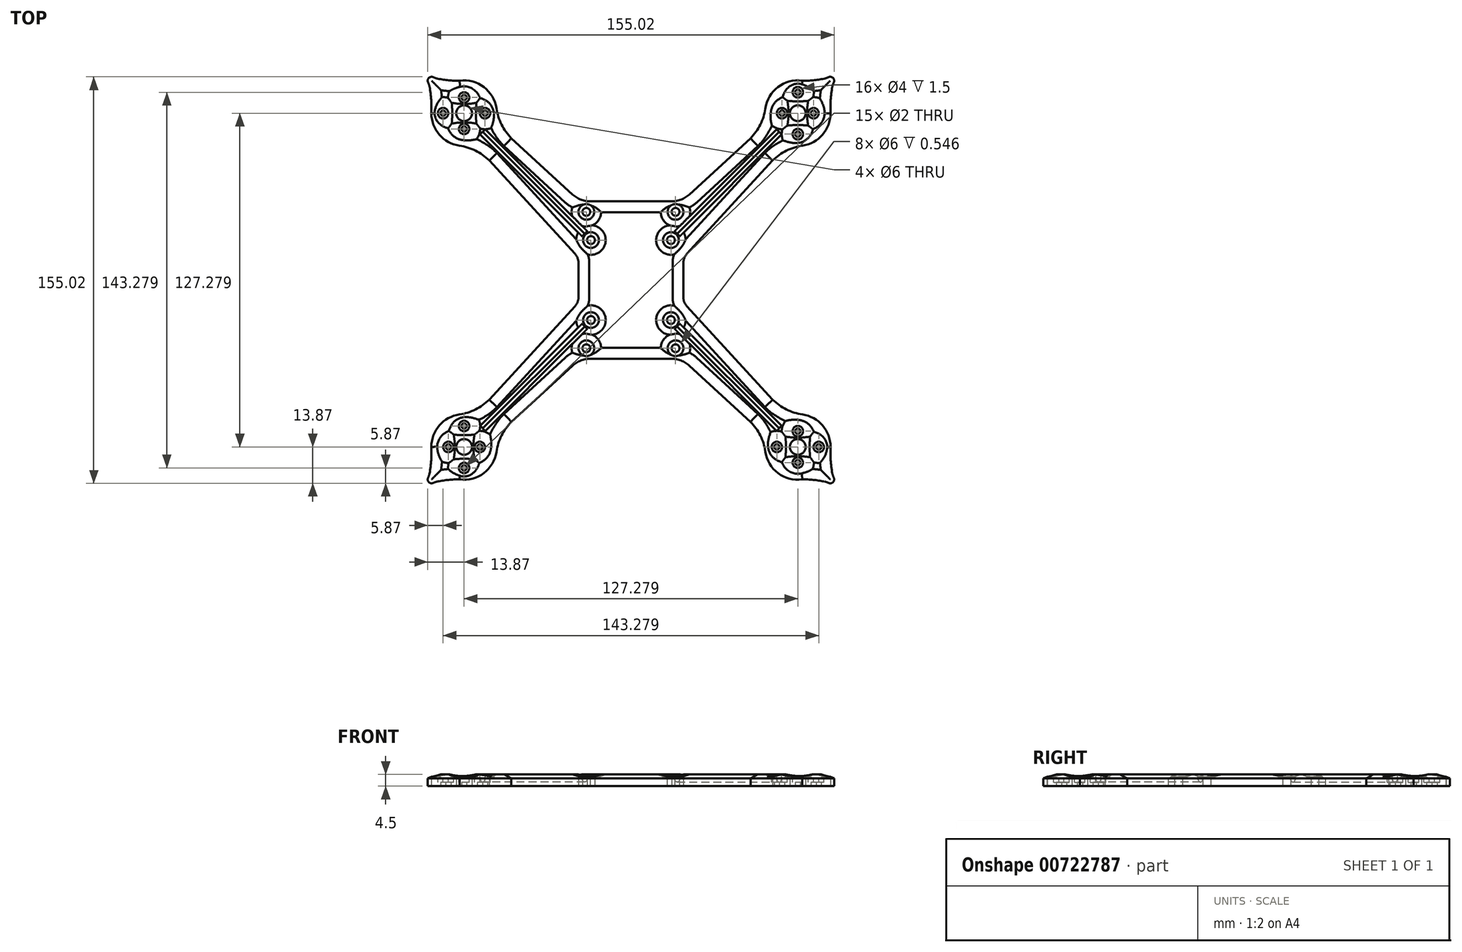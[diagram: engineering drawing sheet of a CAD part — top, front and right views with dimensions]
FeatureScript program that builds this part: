
annotation { "Feature Type Name" : "Feature", "Feature Type Description" : "" }
export const myFeature = defineFeature(function(context is Context, id is Id, definition is map)
    precondition{}
    {
        {
            var Q0;
            Q0=qCreatedBy(makeId("Top.planeOp"),FACE);
            var sketch = newSketch(context, id + "F0", { "sketchPlane" : qUnion([Q0])});
            skCircle(sketch, "E0", {"center": v(0, 0) * mm, "radius": 90 * mm, "construction": true});
            skLineSegment(sketch, "E1", {"start": v(0, 0) * mm, "end": v(63.64, 63.64) * mm, "construction": true});
            skCircle(sketch, "E2", {"center": v(63.64, 63.64) * mm, "radius": 51 * mm, "construction": true});
            skLineSegment(sketch, "E3", {"start": v(72.48, 54.8) * mm, "end": v(54.8, 72.48) * mm, "construction": true});
            skLineSegment(sketch, "E4", {"start": v(63.64, 49.27) * mm, "end": v(63.64, 78) * mm, "construction": true});
            skLineSegment(sketch, "E5", {"start": v(39.58, 63.64) * mm, "end": v(75.05, 63.64) * mm, "construction": true});
            skCircle(sketch, "E6", {"center": v(63.64, 63.64) * mm, "radius": 6 * mm, "construction": true});
            skCircle(sketch, "E7", {"center": v(63.64, 63.64) * mm, "radius": 8 * mm, "construction": true});
            skCircle(sketch, "E8", {"center": v(71.64, 63.64) * mm, "radius": 1 * mm, "construction": true});
            skCircle(sketch, "E9", {"center": v(55.64, 63.64) * mm, "radius": 1 * mm, "construction": true});
            skCircle(sketch, "E10", {"center": v(63.64, 69.64) * mm, "radius": 1 * mm, "construction": true});
            skCircle(sketch, "E11", {"center": v(63.64, 57.64) * mm, "radius": 1 * mm, "construction": true});
            skLineSegment(sketch, "E12", {"start": v(45.6, 54.1) * mm, "end": v(19.59, 28.07) * mm, "construction": true});
            skLineSegment(sketch, "E13.MirrorCS", {"start": v(54.1, 45.6) * mm, "end": v(22.86, 14.38) * mm, "construction": true});
            skArc(sketch, "E14", {"start": v(65.4, 51.27) * mm, "mid": v(73.41, 55.85) * mm, "end": v(76.1, 64.68) * mm});
            skPoint(sketch, "E15.visualSharp", {"position": v(60.13, 51.64) * mm});
            skArc(sketch, "E15.filletArc", {"start": v(65.4, 51.27) * mm, "mid": v(59.3, 49.35) * mm, "end": v(54.1, 45.6) * mm});
            skPoint(sketch, "E16.visualSharp", {"position": v(51.64, 60.13) * mm});
            skArc(sketch, "E16.filletArc", {"start": v(45.6, 54.1) * mm, "mid": v(49.35, 59.3) * mm, "end": v(51.27, 65.4) * mm});
            skLineSegment(sketch, "E17", {"start": v(72.49, 72.47) * mm, "end": v(76.01, 76.01) * mm, "construction": true});
            skLineSegment(sketch, "E18", {"start": v(61.1, 90.85) * mm, "end": v(75.11, 76.91) * mm, "construction": true});
            skArc(sketch, "E19", {"start": v(77.37, 75.37) * mm, "mid": v(77.07, 77.08) * mm, "end": v(75.36, 77.36) * mm});
            skArc(sketch, "E20", {"start": v(76.81, 73.67) * mm, "mid": v(76.17, 68.67) * mm, "end": v(76.14, 63.64) * mm});
            skArc(sketch, "E21.MirrorCS", {"start": v(73.66, 76.8) * mm, "mid": v(68.67, 76.13) * mm, "end": v(63.64, 76.07) * mm});
            skPoint(sketch, "E22.visualSharp", {"position": v(77.08, 74.96) * mm});
            skArc(sketch, "E22.filletArc", {"start": v(77.37, 75.37) * mm, "mid": v(77.04, 74.54) * mm, "end": v(76.81, 73.67) * mm});
            skPoint(sketch, "E23.visualSharp", {"position": v(74.95, 77.07) * mm});
            skArc(sketch, "E23.filletArc", {"start": v(73.66, 76.8) * mm, "mid": v(74.53, 77.03) * mm, "end": v(75.36, 77.36) * mm});
            skArc(sketch, "E24.trimOffspring", {"start": v(65.35, 76.02) * mm, "mid": v(56.12, 73.62) * mm, "end": v(51.27, 65.4) * mm});
            skCircle(sketch, "E25", {"center": v(63.64, 63.64) * mm, "radius": 3 * mm});
            skLineSegment(sketch, "E26", {"start": v(0, 90) * mm, "end": v(0, -90) * mm, "construction": true});
            skLineSegment(sketch, "E27", {"start": v(-90, 0) * mm, "end": v(90, 0) * mm, "construction": true});
            skArc(sketch, "E28.MirrorCS", {"start": v(-73.66, 76.8) * mm, "mid": v(-74.53, 77.03) * mm, "end": v(-75.36, 77.36) * mm});
            skArc(sketch, "E29.MirrorCS", {"start": v(-77.37, 75.37) * mm, "mid": v(-77.04, 74.54) * mm, "end": v(-76.81, 73.67) * mm});
            skArc(sketch, "E30.MirrorCS", {"start": v(-77.37, 75.37) * mm, "mid": v(-77.07, 77.08) * mm, "end": v(-75.36, 77.36) * mm});
            skCircle(sketch, "E31.MirrorC", {"center": v(-63.64, 57.64) * mm, "radius": 1 * mm});
            skCircle(sketch, "E32.MirrorC", {"center": v(-71.64, 63.64) * mm, "radius": 1 * mm});
            skLineSegment(sketch, "E33.MirrorCS", {"start": v(-72.49, 72.47) * mm, "end": v(-76.01, 76.01) * mm, "construction": true});
            skPoint(sketch, "E34.MirrorP", {"position": v(-77.08, 74.96) * mm});
            skArc(sketch, "E35.MirrorCS", {"start": v(-65.4, 51.27) * mm, "mid": v(-59.3, 49.35) * mm, "end": v(-54.1, 45.6) * mm});
            skCircle(sketch, "E36.MirrorC", {"center": v(-63.64, 69.64) * mm, "radius": 1 * mm});
            skArc(sketch, "E37.MirrorCS", {"start": v(-65.35, 76.02) * mm, "mid": v(-56.12, 73.62) * mm, "end": v(-51.27, 65.4) * mm});
            skArc(sketch, "E38.MirrorCS", {"start": v(-45.6, 54.1) * mm, "mid": v(-49.35, 59.3) * mm, "end": v(-51.27, 65.4) * mm});
            skCircle(sketch, "E39.MirrorC", {"center": v(-63.64, 63.64) * mm, "radius": 3 * mm});
            skArc(sketch, "E40.MirrorCS", {"start": v(-65.4, 51.27) * mm, "mid": v(-73.41, 55.85) * mm, "end": v(-76.1, 64.68) * mm});
            skPoint(sketch, "E41.MirrorP", {"position": v(-74.95, 77.07) * mm});
            skLineSegment(sketch, "E42.MirrorCS", {"start": v(-72.48, 54.8) * mm, "end": v(-54.8, 72.48) * mm, "construction": true});
            skArc(sketch, "E43.MirrorCS", {"start": v(-73.66, 76.8) * mm, "mid": v(-68.67, 76.13) * mm, "end": v(-63.64, 76.07) * mm});
            skCircle(sketch, "E44.MirrorC", {"center": v(-55.64, 63.64) * mm, "radius": 1 * mm});
            skArc(sketch, "E45.MirrorCS", {"start": v(-76.81, 73.67) * mm, "mid": v(-76.17, 68.67) * mm, "end": v(-76.14, 63.64) * mm});
            skLineSegment(sketch, "E46.MirrorCS", {"start": v(-63.64, 49.27) * mm, "end": v(-63.64, 78) * mm, "construction": true});
            skPoint(sketch, "E47.MirrorP", {"position": v(-51.64, 60.13) * mm});
            skLineSegment(sketch, "E48.MirrorCS", {"start": v(0, 0) * mm, "end": v(-63.64, 63.64) * mm, "construction": true});
            skLineSegment(sketch, "E49.MirrorCS", {"start": v(-39.58, 63.64) * mm, "end": v(-68.38, 63.64) * mm, "construction": true});
            skLineSegment(sketch, "E50.MirrorCS", {"start": v(-45.6, 54.1) * mm, "end": v(-19.59, 28.07) * mm, "construction": true});
            skLineSegment(sketch, "E51.MirrorCS", {"start": v(-61.1, 90.85) * mm, "end": v(-75.11, 76.91) * mm, "construction": true});
            skCircle(sketch, "E52.MirrorC", {"center": v(-63.64, 63.64) * mm, "radius": 8 * mm, "construction": true});
            skLineSegment(sketch, "E53.MirrorCS", {"start": v(-54.1, 45.6) * mm, "end": v(-22.86, 14.38) * mm, "construction": true});
            skPoint(sketch, "E54.MirrorP", {"position": v(-60.13, 51.64) * mm});
            skCircle(sketch, "E55.MirrorC", {"center": v(-63.64, 63.64) * mm, "radius": 51 * mm, "construction": true});
            skCircle(sketch, "E56.MirrorC", {"center": v(-63.64, 63.64) * mm, "radius": 6 * mm, "construction": true});
            skLineSegment(sketch, "E57.bottom", {"start": v(15.25, 15.25) * mm, "end": v(-15.25, 15.25) * mm, "construction": true});
            skLineSegment(sketch, "E57.top", {"start": v(15.25, -15.25) * mm, "end": v(-15.25, -15.25) * mm, "construction": true});
            skLineSegment(sketch, "E57.left", {"start": v(15.25, 15.25) * mm, "end": v(15.25, -15.25) * mm, "construction": true});
            skLineSegment(sketch, "E57.right", {"start": v(-15.25, 15.25) * mm, "end": v(-15.25, -15.25) * mm, "construction": true});
            skCircle(sketch, "E58", {"center": v(-15.25, 15.25) * mm, "radius": 1.5 * mm});
            skCircle(sketch, "E59", {"center": v(15.25, 15.25) * mm, "radius": 1.5 * mm});
            skCircle(sketch, "E60", {"center": v(15.25, -15.25) * mm, "radius": 1.5 * mm});
            skCircle(sketch, "E61", {"center": v(-15.25, -15.25) * mm, "radius": 1.5 * mm});
            skLineSegment(sketch, "E62.bottom", {"start": v(-17.5, 17.5) * mm, "end": v(17.5, 17.5) * mm, "construction": true});
            skLineSegment(sketch, "E62.top", {"start": v(-17.5, -17.5) * mm, "end": v(17.5, -17.5) * mm, "construction": true});
            skLineSegment(sketch, "E62.left", {"start": v(-17.5, 17.5) * mm, "end": v(-17.5, -17.5) * mm, "construction": true});
            skLineSegment(sketch, "E62.right", {"start": v(17.5, 17.5) * mm, "end": v(17.5, -17.5) * mm, "construction": true});
            skLineSegment(sketch, "E63.bottom", {"start": v(19.37, -30) * mm, "end": v(-19.37, -30) * mm});
            skLineSegment(sketch, "E63.left", {"start": v(20, -6.54) * mm, "end": v(20, 6.54) * mm});
            skLineSegment(sketch, "E63.right", {"start": v(-20, -6.54) * mm, "end": v(-20, 6.54) * mm});
            skPoint(sketch, "E64.visualSharp", {"position": v(-20, -30) * mm});
            skPoint(sketch, "E65.visualSharp", {"position": v(20, -30) * mm});
            skLineSegment(sketch, "E66.bottom", {"start": v(17, -26) * mm, "end": v(-17, -26) * mm});
            skLineSegment(sketch, "E66.top", {"start": v(17, 26) * mm, "end": v(-17, 26) * mm});
            skLineSegment(sketch, "E66.left", {"start": v(17, -26) * mm, "end": v(17, 26) * mm});
            skLineSegment(sketch, "E66.right", {"start": v(-17, -26) * mm, "end": v(-17, 26) * mm});
            skCircle(sketch, "E67", {"center": v(17, 26) * mm, "radius": 1.5 * mm});
            skCircle(sketch, "E68", {"center": v(-17, 26) * mm, "radius": 1.5 * mm});
            skCircle(sketch, "E69", {"center": v(17, -26) * mm, "radius": 1.5 * mm});
            skCircle(sketch, "E70", {"center": v(-17, -26) * mm, "radius": 1.5 * mm});
            skLineSegment(sketch, "E71", {"start": v(-54.1, 45.6) * mm, "end": v(-21.32, 9.92) * mm});
            skPoint(sketch, "E72.visualSharp", {"position": v(-20, 8.49) * mm});
            skArc(sketch, "E72.filletArc", {"start": v(-20, 6.54) * mm, "mid": v(-20.34, 8.35) * mm, "end": v(-21.32, 9.92) * mm});
            skLineSegment(sketch, "E73.MirrorCS", {"start": v(-45.6, 54.1) * mm, "end": v(-22.24, 32.63) * mm});
            skArc(sketch, "E74.MirrorCS", {"start": v(20, 6.54) * mm, "mid": v(20.34, 8.35) * mm, "end": v(21.32, 9.92) * mm});
            skLineSegment(sketch, "E75.MirrorCS", {"start": v(45.6, 54.1) * mm, "end": v(22.24, 32.63) * mm});
            skLineSegment(sketch, "E76.MirrorCS", {"start": v(54.1, 45.6) * mm, "end": v(21.32, 9.92) * mm});
            skArc(sketch, "E77.MirrorCS", {"start": v(-20, -6.54) * mm, "mid": v(-20.34, -8.35) * mm, "end": v(-21.32, -9.92) * mm});
            skArc(sketch, "E78.MirrorCS", {"start": v(20, -6.54) * mm, "mid": v(20.34, -8.35) * mm, "end": v(21.32, -9.92) * mm});
            skLineSegment(sketch, "E79.MirrorCS", {"start": v(15.48, 30) * mm, "end": v(-15.48, 30) * mm});
            skPoint(sketch, "E80.orphan", {"position": v(-16.01, -30) * mm});
            skPoint(sketch, "E81.orphan", {"position": v(16.01, -30) * mm});
            skPoint(sketch, "E82.newPointB", {"position": v(9.92, 21.32) * mm});
            skArc(sketch, "E82.filletArc", {"start": v(15.48, 30) * mm, "mid": v(19.1, 30.68) * mm, "end": v(22.24, 32.63) * mm});
            skPoint(sketch, "E83.newPointA", {"position": v(-9.92, 21.32) * mm});
            skArc(sketch, "E83.filletArc", {"start": v(-22.24, 32.63) * mm, "mid": v(-19.1, 30.68) * mm, "end": v(-15.48, 30) * mm});
            skLineSegment(sketch, "E84.MirrorCS", {"start": v(54.1, -45.6) * mm, "end": v(21.32, -9.92) * mm});
            skLineSegment(sketch, "E85.MirrorCS", {"start": v(54.1, -45.6) * mm, "end": v(22.86, -14.38) * mm, "construction": true});
            skLineSegment(sketch, "E86.MirrorCS", {"start": v(-54.1, -45.6) * mm, "end": v(-21.32, -9.92) * mm});
            skLineSegment(sketch, "E87.MirrorCS", {"start": v(-54.1, -45.6) * mm, "end": v(-22.86, -14.38) * mm, "construction": true});
            skLineSegment(sketch, "E88.MirrorCS", {"start": v(0, 0) * mm, "end": v(-63.64, -63.64) * mm, "construction": true});
            skLineSegment(sketch, "E89.MirrorCS", {"start": v(-45.6, -54.1) * mm, "end": v(-19.59, -28.07) * mm, "construction": true});
            skCircle(sketch, "E90.MirrorC", {"center": v(-63.64, -63.64) * mm, "radius": 51 * mm, "construction": true});
            skCircle(sketch, "E91.MirrorC", {"center": v(63.64, -63.64) * mm, "radius": 51 * mm, "construction": true});
            skLineSegment(sketch, "E92.MirrorCS", {"start": v(45.6, -54.1) * mm, "end": v(19.59, -28.07) * mm, "construction": true});
            skLineSegment(sketch, "E93.MirrorCS", {"start": v(0, 0) * mm, "end": v(63.64, -63.64) * mm, "construction": true});
            skArc(sketch, "E94.MirrorCS", {"start": v(73.66, -76.8) * mm, "mid": v(74.53, -77.03) * mm, "end": v(75.36, -77.36) * mm});
            skArc(sketch, "E95.MirrorCS", {"start": v(77.37, -75.37) * mm, "mid": v(77.07, -77.08) * mm, "end": v(75.36, -77.36) * mm});
            skArc(sketch, "E96.MirrorCS", {"start": v(-77.37, -75.37) * mm, "mid": v(-77.04, -74.54) * mm, "end": v(-76.81, -73.67) * mm});
            skArc(sketch, "E97.MirrorCS", {"start": v(-73.66, -76.8) * mm, "mid": v(-74.53, -77.03) * mm, "end": v(-75.36, -77.36) * mm});
            skArc(sketch, "E98.MirrorCS", {"start": v(-77.37, -75.37) * mm, "mid": v(-77.07, -77.08) * mm, "end": v(-75.36, -77.36) * mm});
            skArc(sketch, "E99.MirrorCS", {"start": v(77.37, -75.37) * mm, "mid": v(77.04, -74.54) * mm, "end": v(76.81, -73.67) * mm});
            skLineSegment(sketch, "E100.MirrorCS", {"start": v(-72.49, -72.47) * mm, "end": v(-76.01, -76.01) * mm, "construction": true});
            skCircle(sketch, "E101.MirrorC", {"center": v(71.64, -63.64) * mm, "radius": 1 * mm});
            skLineSegment(sketch, "E102.MirrorCS", {"start": v(72.49, -72.47) * mm, "end": v(76.01, -76.01) * mm, "construction": true});
            skArc(sketch, "E103.MirrorCS", {"start": v(-22.24, -32.63) * mm, "mid": v(-19.1, -30.68) * mm, "end": v(-15.48, -30) * mm});
            skCircle(sketch, "E104.MirrorC", {"center": v(63.64, -63.64) * mm, "radius": 3 * mm});
            skArc(sketch, "E105.MirrorCS", {"start": v(15.48, -30) * mm, "mid": v(19.1, -30.68) * mm, "end": v(22.24, -32.63) * mm});
            skCircle(sketch, "E106.MirrorC", {"center": v(-63.64, -57.64) * mm, "radius": 1 * mm, "construction": true});
            skCircle(sketch, "E107.MirrorC", {"center": v(63.64, -57.64) * mm, "radius": 1 * mm});
            skArc(sketch, "E108.MirrorCS", {"start": v(-45.6, -54.1) * mm, "mid": v(-49.35, -59.3) * mm, "end": v(-51.27, -65.4) * mm});
            skCircle(sketch, "E109.MirrorC", {"center": v(55.64, -63.64) * mm, "radius": 1 * mm});
            skArc(sketch, "E110.MirrorCS", {"start": v(65.4, -51.27) * mm, "mid": v(59.3, -49.35) * mm, "end": v(54.1, -45.6) * mm});
            skCircle(sketch, "E111.MirrorC", {"center": v(-55.64, -63.64) * mm, "radius": 1 * mm, "construction": true});
            skArc(sketch, "E112.MirrorCS", {"start": v(-65.4, -51.27) * mm, "mid": v(-59.3, -49.35) * mm, "end": v(-54.1, -45.6) * mm});
            skLineSegment(sketch, "E113.MirrorCS", {"start": v(72.48, -54.8) * mm, "end": v(54.8, -72.48) * mm, "construction": true});
            skArc(sketch, "E114.MirrorCS", {"start": v(65.35, -76.02) * mm, "mid": v(56.12, -73.62) * mm, "end": v(51.27, -65.4) * mm});
            skArc(sketch, "E115.MirrorCS", {"start": v(65.4, -51.27) * mm, "mid": v(73.41, -55.85) * mm, "end": v(76.1, -64.68) * mm});
            skCircle(sketch, "E116.MirrorC", {"center": v(-63.64, -69.64) * mm, "radius": 1 * mm, "construction": true});
            skArc(sketch, "E117.MirrorCS", {"start": v(76.81, -73.67) * mm, "mid": v(76.17, -68.67) * mm, "end": v(76.14, -63.64) * mm});
            skArc(sketch, "E118.MirrorCS", {"start": v(73.66, -76.8) * mm, "mid": v(68.67, -76.13) * mm, "end": v(63.64, -76.07) * mm});
            skArc(sketch, "E119.MirrorCS", {"start": v(45.6, -54.1) * mm, "mid": v(49.35, -59.3) * mm, "end": v(51.27, -65.4) * mm});
            skPoint(sketch, "E120.MirrorP", {"position": v(74.95, -77.07) * mm});
            skCircle(sketch, "E121.MirrorC", {"center": v(63.64, -69.64) * mm, "radius": 1 * mm});
            skCircle(sketch, "E122.MirrorC", {"center": v(-63.64, -63.64) * mm, "radius": 3 * mm});
            skPoint(sketch, "E123.MirrorP", {"position": v(77.08, -74.96) * mm});
            skCircle(sketch, "E124.MirrorC", {"center": v(-71.64, -63.64) * mm, "radius": 1 * mm, "construction": true});
            skLineSegment(sketch, "E125.MirrorCS", {"start": v(-63.64, -49.27) * mm, "end": v(-63.64, -78) * mm, "construction": true});
            skLineSegment(sketch, "E126.MirrorCS", {"start": v(63.64, -49.27) * mm, "end": v(63.64, -78) * mm, "construction": true});
            skLineSegment(sketch, "E127.MirrorCS", {"start": v(-72.48, -54.8) * mm, "end": v(-54.8, -72.48) * mm, "construction": true});
            skCircle(sketch, "E128.MirrorC", {"center": v(63.64, -63.64) * mm, "radius": 6 * mm, "construction": true});
            skPoint(sketch, "E129.MirrorP", {"position": v(-77.08, -74.96) * mm});
            skPoint(sketch, "E130.MirrorP", {"position": v(-51.64, -60.13) * mm});
            skLineSegment(sketch, "E131.MirrorCS", {"start": v(15.48, -30) * mm, "end": v(-15.48, -30) * mm});
            skArc(sketch, "E132.MirrorCS", {"start": v(-65.35, -76.02) * mm, "mid": v(-56.12, -73.62) * mm, "end": v(-51.27, -65.4) * mm});
            skLineSegment(sketch, "E133.MirrorCS", {"start": v(-61.1, -90.85) * mm, "end": v(-75.11, -76.91) * mm, "construction": true});
            skCircle(sketch, "E134.MirrorC", {"center": v(-63.64, -63.64) * mm, "radius": 8 * mm, "construction": true});
            skPoint(sketch, "E135.MirrorP", {"position": v(-60.13, -51.64) * mm});
            skArc(sketch, "E136.MirrorCS", {"start": v(-65.4, -51.27) * mm, "mid": v(-73.41, -55.85) * mm, "end": v(-76.1, -64.68) * mm});
            skLineSegment(sketch, "E137.MirrorCS", {"start": v(45.6, -54.1) * mm, "end": v(22.24, -32.63) * mm});
            skCircle(sketch, "E138.MirrorC", {"center": v(63.64, -63.64) * mm, "radius": 8 * mm, "construction": true});
            skLineSegment(sketch, "E139.MirrorCS", {"start": v(-39.58, -63.64) * mm, "end": v(-74.66, -63.64) * mm, "construction": true});
            skPoint(sketch, "E140.MirrorP", {"position": v(51.64, -60.13) * mm});
            skArc(sketch, "E141.MirrorCS", {"start": v(-76.81, -73.67) * mm, "mid": v(-76.17, -68.67) * mm, "end": v(-76.14, -63.64) * mm});
            skPoint(sketch, "E142.MirrorP", {"position": v(-74.95, -77.07) * mm});
            skArc(sketch, "E143.MirrorCS", {"start": v(-73.66, -76.8) * mm, "mid": v(-68.67, -76.13) * mm, "end": v(-63.64, -76.07) * mm});
            skLineSegment(sketch, "E144.MirrorCS", {"start": v(-45.6, -54.1) * mm, "end": v(-22.24, -32.63) * mm});
            skPoint(sketch, "E145.MirrorP", {"position": v(60.13, -51.64) * mm});
            skLineSegment(sketch, "E146.MirrorCS", {"start": v(39.58, -63.64) * mm, "end": v(68.38, -63.64) * mm, "construction": true});
            skLineSegment(sketch, "E147.MirrorCS", {"start": v(61.1, -90.85) * mm, "end": v(75.11, -76.91) * mm, "construction": true});
            skCircle(sketch, "E148.MirrorC", {"center": v(-63.64, -63.64) * mm, "radius": 6 * mm, "construction": true});
            skCircle(sketch, "E149", {"center": v(63.64, 71.64) * mm, "radius": 1 * mm});
            skCircle(sketch, "E150", {"center": v(63.64, 55.64) * mm, "radius": 1 * mm});
            skCircle(sketch, "E151", {"center": v(57.64, 63.64) * mm, "radius": 1.03 * mm});
            skPoint(sketch, "E152.orphan", {"position": v(68.38, 63.64) * mm});
            skCircle(sketch, "E153", {"center": v(69.64, 63.64) * mm, "radius": 1 * mm});
            skCircle(sketch, "E154", {"center": v(-63.64, -55.64) * mm, "radius": 1 * mm});
            skCircle(sketch, "E155", {"center": v(-63.64, -71.64) * mm, "radius": 1 * mm});
            skCircle(sketch, "E156", {"center": v(-57.64, -63.64) * mm, "radius": 1 * mm});
            skPoint(sketch, "E157.orphan", {"position": v(-68.38, -63.64) * mm});
            skCircle(sketch, "E158", {"center": v(-69.64, -63.64) * mm, "radius": 1 * mm});
            skSolve(sketch);
        }
        {
            var Q0;
            {var subQ6=sQuery(id+"F0.wireOp",EDGE,"7082ca94-923b-4291-9ee5-27a8198b0ac30.MirrorCS");Q0=makeQuery(id+"F0.imprint","IMPRINT",FACE,{"disambiguationData":[TD([[makeQuery(id+"F0.imprint","IMPRINT",EDGE,{"derivedFrom":subQ6}),1.0]])]});}
            var Q1;
            Q1=makeQuery(id+"F0.imprint","IMPRINT",FACE,{"disambiguationData":[TD([[makeQuery(id+"F0.imprint","IMPRINT",EDGE,{"derivedFrom":sQuery(id+"F0.wireOp",EDGE,"gLzA5nj6-a7D7-01xJ-Imyk-9g7RHIkeMFTe")}),-1.0]])]});
            var Q2;
            Q2=makeQuery(id+"F0.imprint","IMPRINT",FACE,{"disambiguationData":[TD([[makeQuery(id+"F0.imprint","IMPRINT",EDGE,{"derivedFrom":sQuery(id+"F0.wireOp",EDGE,"E8")}),-1.0]])]});
            var Q3;
            {var subQ1=sQuery(id+"F0.wireOp",EDGE,"2743e663-3ea0-48b2-b3a6-c681f6d0d95d0.MirrorCS");Q3=makeQuery(id+"F0.imprint","IMPRINT",FACE,{"disambiguationData":[TD([[makeQuery(id+"F0.imprint","IMPRINT",EDGE,{"derivedFrom":subQ1}),1.0]])]});}
            var Q4;
            {var subQ3=sQuery(id+"F0.wireOp",EDGE,"7082ca94-923b-4291-9ee5-27a8198b0ac32.MirrorCS");Q4=makeQuery(id+"F0.imprint","IMPRINT",FACE,{"disambiguationData":[TD([[makeQuery(id+"F0.imprint","IMPRINT",EDGE,{"derivedFrom":subQ3}),-1.0]])]});}
            var Q5;
            {var subQ0=sQuery(id+"F0.wireOp",EDGE,"jrIIyoHM-jgcZ-u3ag-vO0J-Hrb3xtMqW8uY");var subQ1=sQuery(id+"F0.wireOp",EDGE,"4ae0184f-0293-4d57-be5d-3c11781dc31c.trimOffspring");var subQ2=makeQuery(id+"F0.imprint","INTERSECT",VERTEX,{"disambiguationData":[OD(0.0)],"derivedFrom":[subQ1,subQ0]});Q5=makeQuery(id+"F0.imprint","IMPRINT",FACE,{"disambiguationData":[TD([[makeQuery(id+"F0.imprint","IMPRINT",EDGE,{"disambiguationData":[TD([[subQ2,-1.0]])],"derivedFrom":subQ1}),-1.0]])]});}
            var Q6;
            {var subQ0=sQuery(id+"F0.wireOp",EDGE,"4ZQ3HuPE-oKdW-LSRt-Dwqu-7NxqxxyVispN");var subQ1=sQuery(id+"F0.wireOp",EDGE,"4ae0184f-0293-4d57-be5d-3c11781dc31c.trimOffspring");var subQ2=makeQuery(id+"F0.imprint","INTERSECT",VERTEX,{"derivedFrom":[subQ1,subQ0]});Q6=makeQuery(id+"F0.imprint","IMPRINT",FACE,{"disambiguationData":[TD([[makeQuery(id+"F0.imprint","IMPRINT",EDGE,{"disambiguationData":[TD([[subQ2,-1.0]])],"derivedFrom":subQ1}),-1.0]])]});}
            var Q7;
            Q7=makeQuery(id+"F0.imprint","IMPRINT",FACE,{"disambiguationData":[TD([[makeQuery(id+"F0.imprint","IMPRINT",EDGE,{"derivedFrom":sQuery(id+"F0.wireOp",EDGE,"E58")}),-1.0]])]});
            var Q8;
            {var subQ32=sQuery(id+"F0.wireOp",EDGE,"E15.filletArc");Q8=makeQuery(id+"F0.imprint","IMPRINT",FACE,{"disambiguationData":[TD([[makeQuery(id+"F0.imprint","IMPRINT",EDGE,{"derivedFrom":subQ32}),-1.0]])]});}
            extrude(context, id + "F1", {"entities" : qUnion([Q0, Q1, Q2, Q3, Q4, Q5, Q6, Q7, Q8]), "depth" : 3 * mm, "offsetDistance" : 25 * mm});
        }
        {
            var Q0;
            {var subQ0=sQuery(id+"F0.wireOp",EDGE,"E73.MirrorCS");var subQ1=sQuery(id+"F0.wireOp",EDGE,"E72.filletArc");var subQ2=sQuery(id+"F0.wireOp",EDGE,"E71");var subQ3=sQuery(id+"F0.wireOp",EDGE,"E70");var subQ4=sQuery(id+"F0.wireOp",EDGE,"E158");var subQ5=sQuery(id+"F0.wireOp",EDGE,"E156");var subQ6=sQuery(id+"F0.wireOp",EDGE,"E155");var subQ7=sQuery(id+"F0.wireOp",EDGE,"E154");var subQ8=sQuery(id+"F0.wireOp",EDGE,"E153");var subQ9=sQuery(id+"F0.wireOp",EDGE,"E151");var subQ10=sQuery(id+"F0.wireOp",EDGE,"E150");var subQ11=sQuery(id+"F0.wireOp",EDGE,"E149");var subQ12=sQuery(id+"F0.wireOp",EDGE,"E144.MirrorCS");var subQ13=sQuery(id+"F0.wireOp",EDGE,"E143.MirrorCS");var subQ14=sQuery(id+"F0.wireOp",EDGE,"E141.MirrorCS");var subQ15=sQuery(id+"F0.wireOp",EDGE,"E137.MirrorCS");var subQ16=sQuery(id+"F0.wireOp",EDGE,"E136.MirrorCS");var subQ17=sQuery(id+"F0.wireOp",EDGE,"E132.MirrorCS");var subQ18=sQuery(id+"F0.wireOp",EDGE,"E131.MirrorCS");var subQ19=sQuery(id+"F0.wireOp",EDGE,"E122.MirrorC");var subQ20=sQuery(id+"F0.wireOp",EDGE,"E121.MirrorC");var subQ21=sQuery(id+"F0.wireOp",EDGE,"E119.MirrorCS");var subQ22=sQuery(id+"F0.wireOp",EDGE,"E118.MirrorCS");var subQ23=sQuery(id+"F0.wireOp",EDGE,"E117.MirrorCS");var subQ24=sQuery(id+"F0.wireOp",EDGE,"E115.MirrorCS");var subQ25=sQuery(id+"F0.wireOp",EDGE,"E114.MirrorCS");var subQ26=sQuery(id+"F0.wireOp",EDGE,"E112.MirrorCS");var subQ27=sQuery(id+"F0.wireOp",EDGE,"E110.MirrorCS");var subQ28=sQuery(id+"F0.wireOp",EDGE,"E109.MirrorC");var subQ29=sQuery(id+"F0.wireOp",EDGE,"E108.MirrorCS");var subQ30=sQuery(id+"F0.wireOp",EDGE,"E107.MirrorC");var subQ31=sQuery(id+"F0.wireOp",EDGE,"E105.MirrorCS");var subQ32=sQuery(id+"F0.wireOp",EDGE,"E104.MirrorC");var subQ33=sQuery(id+"F0.wireOp",EDGE,"E103.MirrorCS");var subQ34=sQuery(id+"F0.wireOp",EDGE,"E101.MirrorC");var subQ35=sQuery(id+"F0.wireOp",EDGE,"E99.MirrorCS");var subQ36=sQuery(id+"F0.wireOp",EDGE,"E98.MirrorCS");var subQ37=sQuery(id+"F0.wireOp",EDGE,"E97.MirrorCS");var subQ38=sQuery(id+"F0.wireOp",EDGE,"E63.right");var subQ39=sQuery(id+"F0.wireOp",EDGE,"E40.MirrorCS");var subQ40=sQuery(id+"F0.wireOp",EDGE,"E63.left");var subQ41=sQuery(id+"F0.wireOp",EDGE,"E39.MirrorC");var subQ42=sQuery(id+"F0.wireOp",EDGE,"E38.MirrorCS");var subQ43=sQuery(id+"F0.wireOp",EDGE,"E37.MirrorCS");var subQ44=sQuery(id+"F0.wireOp",EDGE,"E36.MirrorC");var subQ45=sQuery(id+"F0.wireOp",EDGE,"E35.MirrorCS");var subQ46=sQuery(id+"F0.wireOp",EDGE,"E32.MirrorC");var subQ47=sQuery(id+"F0.wireOp",EDGE,"E31.MirrorC");var subQ48=sQuery(id+"F0.wireOp",EDGE,"E30.MirrorCS");var subQ49=sQuery(id+"F0.wireOp",EDGE,"E29.MirrorCS");var subQ50=sQuery(id+"F0.wireOp",EDGE,"E28.MirrorCS");var subQ51=sQuery(id+"F0.wireOp",EDGE,"E16.filletArc");var subQ52=sQuery(id+"F0.wireOp",EDGE,"E96.MirrorCS");var subQ53=sQuery(id+"F0.wireOp",EDGE,"E15.filletArc");var subQ54=sQuery(id+"F0.wireOp",EDGE,"E95.MirrorCS");var subQ55=sQuery(id+"F0.wireOp",EDGE,"E19");var subQ56=sQuery(id+"F0.wireOp",EDGE,"E67");var subQ57=sQuery(id+"F0.wireOp",EDGE,"E43.MirrorCS");var subQ58=sQuery(id+"F0.wireOp",EDGE,"E14");var subQ59=sQuery(id+"F0.wireOp",EDGE,"E84.MirrorCS");var subQ60=sQuery(id+"F0.wireOp",EDGE,"E25");var subQ61=sQuery(id+"F0.wireOp",EDGE,"E20");var subQ62=sQuery(id+"F0.wireOp",EDGE,"E21.MirrorCS");var subQ63=sQuery(id+"F0.wireOp",EDGE,"E22.filletArc");var subQ64=sQuery(id+"F0.wireOp",EDGE,"E23.filletArc");var subQ65=sQuery(id+"F0.wireOp",EDGE,"E24.trimOffspring");var subQ66=sQuery(id+"F0.wireOp",EDGE,"E68");var subQ67=sQuery(id+"F0.wireOp",EDGE,"E44.MirrorC");var subQ68=sQuery(id+"F0.wireOp",EDGE,"E69");var subQ69=sQuery(id+"F0.wireOp",EDGE,"E45.MirrorCS");var subQ70=sQuery(id+"F0.wireOp",EDGE,"E74.MirrorCS");var subQ71=sQuery(id+"F0.wireOp",EDGE,"E75.MirrorCS");var subQ72=sQuery(id+"F0.wireOp",EDGE,"E76.MirrorCS");var subQ73=sQuery(id+"F0.wireOp",EDGE,"E77.MirrorCS");var subQ74=sQuery(id+"F0.wireOp",EDGE,"E78.MirrorCS");var subQ75=sQuery(id+"F0.wireOp",EDGE,"E79.MirrorCS");var subQ76=sQuery(id+"F0.wireOp",EDGE,"E82.filletArc");var subQ77=sQuery(id+"F0.wireOp",EDGE,"E83.filletArc");var subQ78=sQuery(id+"F0.wireOp",EDGE,"E86.MirrorCS");var subQ79=sQuery(id+"F0.wireOp",EDGE,"E94.MirrorCS");Q0=makeQuery(id+"FJsL77OAOiJxj8z_1.boolean.opBoolean","SPLIT",FACE,{"disambiguationData":[TD([makeQuery(id+"F1.opExtrude","SWEPT_FACE",FACE,{"disambiguationData":[OSD([subQ58])]})])],"derivedFrom":makeQuery(id+"F1.opExtrude","CAP_FACE",FACE,{"disambiguationData":[OSD([subQ58,subQ53,subQ51,subQ55,subQ61,subQ62,subQ63,subQ64,subQ65,subQ60,subQ50,subQ49,subQ48,subQ47,subQ46,subQ45,subQ44,subQ43,subQ42,subQ41,subQ39,subQ57,subQ67,subQ69,sQuery(id+"F0.wireOp",EDGE,"E58"),sQuery(id+"F0.wireOp",EDGE,"E59"),sQuery(id+"F0.wireOp",EDGE,"E60"),sQuery(id+"F0.wireOp",EDGE,"E61"),subQ40,subQ38,subQ56,subQ66,subQ68,subQ3,subQ2,subQ1,subQ0,subQ70,subQ71,subQ72,subQ73,subQ74,subQ75,subQ76,subQ77,subQ59,subQ78,subQ79,subQ54,subQ52,subQ37,subQ36,subQ35,subQ34,subQ33,subQ32,subQ31,subQ30,subQ29,subQ28,subQ27,subQ26,subQ25,subQ24,subQ23,subQ22,subQ21,subQ20,subQ19,subQ18,subQ17,subQ16,subQ15,subQ14,subQ13,subQ12,subQ11,subQ10,subQ9,subQ8,subQ7,subQ6,subQ5,subQ4])],"isStart":false})});}
            var sketch = newSketch(context, id + "F2", { "sketchPlane" : qUnion([Q0])});
            skCircle(sketch, "E159", {"center": v(-71.64, 63.64) * mm, "radius": 2 * mm});
            skCircle(sketch, "E160", {"center": v(-63.64, 69.64) * mm, "radius": 2 * mm});
            skCircle(sketch, "E161", {"center": v(-55.64, 63.64) * mm, "radius": 2 * mm});
            skCircle(sketch, "E162", {"center": v(-63.64, 57.64) * mm, "radius": 2 * mm});
            skCircle(sketch, "E163", {"center": v(63.64, 71.64) * mm, "radius": 2 * mm});
            skCircle(sketch, "E164", {"center": v(57.64, 63.64) * mm, "radius": 2 * mm});
            skCircle(sketch, "E165", {"center": v(69.64, 63.64) * mm, "radius": 2 * mm});
            skCircle(sketch, "E166", {"center": v(63.64, 55.64) * mm, "radius": 2 * mm});
            skCircle(sketch, "E167", {"center": v(63.64, -57.64) * mm, "radius": 2 * mm});
            skCircle(sketch, "E168", {"center": v(71.64, -63.64) * mm, "radius": 2 * mm});
            skCircle(sketch, "E169", {"center": v(63.64, -69.64) * mm, "radius": 2 * mm});
            skCircle(sketch, "E170", {"center": v(55.64, -63.64) * mm, "radius": 2 * mm});
            skCircle(sketch, "E171", {"center": v(-63.64, -55.64) * mm, "radius": 2 * mm});
            skCircle(sketch, "E172", {"center": v(-57.64, -63.64) * mm, "radius": 2 * mm});
            skCircle(sketch, "E173", {"center": v(-63.64, -71.64) * mm, "radius": 2 * mm});
            skCircle(sketch, "E174", {"center": v(-69.64, -63.64) * mm, "radius": 2 * mm});
            skSolve(sketch);
        }
        {
            var Q0;
            Q0=qSketchRegion(id+"F2",true);
            extrude(context, id + "F3", {"entities" : qUnion([Q0]), "operationType" : NewBodyOperationType.REMOVE, "oppositeDirection" : true, "depth" : 1.5 * mm, "offsetDistance" : 25 * mm});
        }
        {
            var Q0;
            Q0=makeQuery(id+"F1.opExtrude","CAP_FACE",FACE,{"disambiguationData":[OSD([sQuery(id+"F0.wireOp",EDGE,"E14"),sQuery(id+"F0.wireOp",EDGE,"E15.filletArc"),sQuery(id+"F0.wireOp",EDGE,"E16.filletArc"),sQuery(id+"F0.wireOp",EDGE,"E19"),sQuery(id+"F0.wireOp",EDGE,"E20"),sQuery(id+"F0.wireOp",EDGE,"E21.MirrorCS"),sQuery(id+"F0.wireOp",EDGE,"E22.filletArc"),sQuery(id+"F0.wireOp",EDGE,"E23.filletArc"),sQuery(id+"F0.wireOp",EDGE,"E24.trimOffspring"),sQuery(id+"F0.wireOp",EDGE,"E25"),sQuery(id+"F0.wireOp",EDGE,"E28.MirrorCS"),sQuery(id+"F0.wireOp",EDGE,"E29.MirrorCS"),sQuery(id+"F0.wireOp",EDGE,"E30.MirrorCS"),sQuery(id+"F0.wireOp",EDGE,"E31.MirrorC"),sQuery(id+"F0.wireOp",EDGE,"E32.MirrorC"),sQuery(id+"F0.wireOp",EDGE,"E35.MirrorCS"),sQuery(id+"F0.wireOp",EDGE,"E36.MirrorC"),sQuery(id+"F0.wireOp",EDGE,"E37.MirrorCS"),sQuery(id+"F0.wireOp",EDGE,"E38.MirrorCS"),sQuery(id+"F0.wireOp",EDGE,"E39.MirrorC"),sQuery(id+"F0.wireOp",EDGE,"E40.MirrorCS"),sQuery(id+"F0.wireOp",EDGE,"E43.MirrorCS"),sQuery(id+"F0.wireOp",EDGE,"E44.MirrorC"),sQuery(id+"F0.wireOp",EDGE,"E45.MirrorCS"),sQuery(id+"F0.wireOp",EDGE,"E58"),sQuery(id+"F0.wireOp",EDGE,"E59"),sQuery(id+"F0.wireOp",EDGE,"E60"),sQuery(id+"F0.wireOp",EDGE,"E61"),sQuery(id+"F0.wireOp",EDGE,"E63.left"),sQuery(id+"F0.wireOp",EDGE,"E63.right"),sQuery(id+"F0.wireOp",EDGE,"E67"),sQuery(id+"F0.wireOp",EDGE,"E68"),sQuery(id+"F0.wireOp",EDGE,"E69"),sQuery(id+"F0.wireOp",EDGE,"E70"),sQuery(id+"F0.wireOp",EDGE,"E71"),sQuery(id+"F0.wireOp",EDGE,"E72.filletArc"),sQuery(id+"F0.wireOp",EDGE,"E73.MirrorCS"),sQuery(id+"F0.wireOp",EDGE,"E74.MirrorCS"),sQuery(id+"F0.wireOp",EDGE,"E75.MirrorCS"),sQuery(id+"F0.wireOp",EDGE,"E76.MirrorCS"),sQuery(id+"F0.wireOp",EDGE,"E77.MirrorCS"),sQuery(id+"F0.wireOp",EDGE,"E78.MirrorCS"),sQuery(id+"F0.wireOp",EDGE,"E79.MirrorCS"),sQuery(id+"F0.wireOp",EDGE,"E82.filletArc"),sQuery(id+"F0.wireOp",EDGE,"E83.filletArc"),sQuery(id+"F0.wireOp",EDGE,"E84.MirrorCS"),sQuery(id+"F0.wireOp",EDGE,"E86.MirrorCS"),sQuery(id+"F0.wireOp",EDGE,"E94.MirrorCS"),sQuery(id+"F0.wireOp",EDGE,"E95.MirrorCS"),sQuery(id+"F0.wireOp",EDGE,"E96.MirrorCS"),sQuery(id+"F0.wireOp",EDGE,"E97.MirrorCS"),sQuery(id+"F0.wireOp",EDGE,"E98.MirrorCS"),sQuery(id+"F0.wireOp",EDGE,"E99.MirrorCS"),sQuery(id+"F0.wireOp",EDGE,"E101.MirrorC"),sQuery(id+"F0.wireOp",EDGE,"E103.MirrorCS"),sQuery(id+"F0.wireOp",EDGE,"E104.MirrorC"),sQuery(id+"F0.wireOp",EDGE,"E105.MirrorCS"),sQuery(id+"F0.wireOp",EDGE,"E107.MirrorC"),sQuery(id+"F0.wireOp",EDGE,"E108.MirrorCS"),sQuery(id+"F0.wireOp",EDGE,"E109.MirrorC"),sQuery(id+"F0.wireOp",EDGE,"E110.MirrorCS"),sQuery(id+"F0.wireOp",EDGE,"E112.MirrorCS"),sQuery(id+"F0.wireOp",EDGE,"E114.MirrorCS"),sQuery(id+"F0.wireOp",EDGE,"E115.MirrorCS"),sQuery(id+"F0.wireOp",EDGE,"E117.MirrorCS"),sQuery(id+"F0.wireOp",EDGE,"E118.MirrorCS"),sQuery(id+"F0.wireOp",EDGE,"E119.MirrorCS"),sQuery(id+"F0.wireOp",EDGE,"E121.MirrorC"),sQuery(id+"F0.wireOp",EDGE,"E122.MirrorC"),sQuery(id+"F0.wireOp",EDGE,"E131.MirrorCS"),sQuery(id+"F0.wireOp",EDGE,"E132.MirrorCS"),sQuery(id+"F0.wireOp",EDGE,"E136.MirrorCS"),sQuery(id+"F0.wireOp",EDGE,"E137.MirrorCS"),sQuery(id+"F0.wireOp",EDGE,"E141.MirrorCS"),sQuery(id+"F0.wireOp",EDGE,"E143.MirrorCS"),sQuery(id+"F0.wireOp",EDGE,"E144.MirrorCS"),sQuery(id+"F0.wireOp",EDGE,"E149"),sQuery(id+"F0.wireOp",EDGE,"E150"),sQuery(id+"F0.wireOp",EDGE,"E151"),sQuery(id+"F0.wireOp",EDGE,"E153"),sQuery(id+"F0.wireOp",EDGE,"E154"),sQuery(id+"F0.wireOp",EDGE,"E155"),sQuery(id+"F0.wireOp",EDGE,"E156"),sQuery(id+"F0.wireOp",EDGE,"E158")])],"isStart":false});
            var sketch = newSketch(context, id + "F4", { "sketchPlane" : qUnion([Q0])});
            skCircle(sketch, "E175", {"center": v(63.64, -57.64) * mm, "radius": 2 * mm});
            skCircle(sketch, "E176", {"center": v(55.64, -63.64) * mm, "radius": 2 * mm});
            skCircle(sketch, "E177", {"center": v(63.64, -69.64) * mm, "radius": 2 * mm});
            skCircle(sketch, "E178", {"center": v(63.64, 71.64) * mm, "radius": 2 * mm});
            skCircle(sketch, "E179", {"center": v(71.64, -63.64) * mm, "radius": 2 * mm});
            skCircle(sketch, "E180", {"center": v(-55.64, 63.64) * mm, "radius": 2 * mm});
            skCircle(sketch, "E181", {"center": v(-63.64, 69.64) * mm, "radius": 2 * mm});
            skCircle(sketch, "E182", {"center": v(-71.64, 63.64) * mm, "radius": 2 * mm});
            skCircle(sketch, "E183", {"center": v(-63.64, -55.64) * mm, "radius": 2 * mm});
            skCircle(sketch, "E184", {"center": v(69.64, 63.64) * mm, "radius": 2 * mm});
            skCircle(sketch, "E185", {"center": v(57.64, 63.64) * mm, "radius": 2 * mm});
            skCircle(sketch, "E186", {"center": v(63.64, 55.64) * mm, "radius": 2 * mm});
            skCircle(sketch, "E187", {"center": v(-63.64, -71.64) * mm, "radius": 2 * mm});
            skCircle(sketch, "E188", {"center": v(-57.64, -63.64) * mm, "radius": 2 * mm});
            skCircle(sketch, "E189", {"center": v(-69.64, -63.64) * mm, "radius": 2 * mm});
            skCircle(sketch, "E190", {"center": v(-63.64, 57.64) * mm, "radius": 2 * mm});
            skCircle(sketch, "E191", {"center": v(-17, 26) * mm, "radius": 1.5 * mm});
            skCircle(sketch, "E192", {"center": v(17, 26) * mm, "radius": 1.5 * mm});
            skCircle(sketch, "E193", {"center": v(-17, -26) * mm, "radius": 1.5 * mm});
            skCircle(sketch, "E194", {"center": v(-15.25, -15.25) * mm, "radius": 1.5 * mm});
            skCircle(sketch, "E195", {"center": v(15.25, -15.25) * mm, "radius": 1.5 * mm});
            skCircle(sketch, "E196", {"center": v(15.25, 15.25) * mm, "radius": 1.5 * mm});
            skCircle(sketch, "E197", {"center": v(-15.25, 15.25) * mm, "radius": 1.5 * mm});
            skCircle(sketch, "E198", {"center": v(17, -26) * mm, "radius": 1.5 * mm});
            skLineSegment(sketch, "E199", {"start": v(15.48, -30) * mm, "end": v(-15.48, -30) * mm});
            skArc(sketch, "E200", {"start": v(15.48, -30) * mm, "mid": v(19.1, -30.68) * mm, "end": v(22.24, -32.63) * mm});
            skLineSegment(sketch, "E201", {"start": v(45.6, -54.1) * mm, "end": v(22.24, -32.63) * mm});
            skArc(sketch, "E202", {"start": v(45.6, -54.1) * mm, "mid": v(49.35, -59.3) * mm, "end": v(51.27, -65.4) * mm});
            skArc(sketch, "E203", {"start": v(65.35, -76.02) * mm, "mid": v(56.12, -73.62) * mm, "end": v(51.27, -65.4) * mm});
            skArc(sketch, "E204", {"start": v(73.66, -76.8) * mm, "mid": v(69.53, -76.2) * mm, "end": v(65.35, -76.02) * mm});
            skArc(sketch, "E205", {"start": v(73.66, -76.8) * mm, "mid": v(74.53, -77.03) * mm, "end": v(75.36, -77.36) * mm});
            skArc(sketch, "E206", {"start": v(77.37, -75.37) * mm, "mid": v(77.07, -77.08) * mm, "end": v(75.36, -77.36) * mm});
            skArc(sketch, "E207", {"start": v(77.37, -75.37) * mm, "mid": v(77.04, -74.54) * mm, "end": v(76.81, -73.67) * mm});
            skArc(sketch, "E208", {"start": v(76.81, -73.67) * mm, "mid": v(76.17, -68.67) * mm, "end": v(76.14, -63.64) * mm});
            skArc(sketch, "E209", {"start": v(65.4, -51.27) * mm, "mid": v(73.08, -55.45) * mm, "end": v(76.14, -63.64) * mm});
            skArc(sketch, "E210", {"start": v(65.4, -51.27) * mm, "mid": v(59.3, -49.35) * mm, "end": v(54.1, -45.6) * mm});
            skLineSegment(sketch, "E211", {"start": v(54.1, -45.6) * mm, "end": v(21.32, -9.92) * mm});
            skArc(sketch, "E212", {"start": v(20, -6.54) * mm, "mid": v(20.34, -8.35) * mm, "end": v(21.32, -9.92) * mm});
            skLineSegment(sketch, "E213", {"start": v(20, -6.54) * mm, "end": v(20, 6.54) * mm});
            skArc(sketch, "E214", {"start": v(20, 6.54) * mm, "mid": v(20.34, 8.35) * mm, "end": v(21.32, 9.92) * mm});
            skLineSegment(sketch, "E215", {"start": v(54.1, 45.6) * mm, "end": v(21.32, 9.92) * mm});
            skArc(sketch, "E216", {"start": v(65.4, 51.27) * mm, "mid": v(59.3, 49.35) * mm, "end": v(54.1, 45.6) * mm});
            skArc(sketch, "E217", {"start": v(65.4, 51.27) * mm, "mid": v(73.08, 55.45) * mm, "end": v(76.14, 63.64) * mm});
            skArc(sketch, "E218", {"start": v(76.81, 73.67) * mm, "mid": v(76.17, 68.67) * mm, "end": v(76.14, 63.64) * mm});
            skArc(sketch, "E219", {"start": v(77.37, 75.37) * mm, "mid": v(77.04, 74.54) * mm, "end": v(76.81, 73.67) * mm});
            skArc(sketch, "E220", {"start": v(77.37, 75.37) * mm, "mid": v(77.07, 77.08) * mm, "end": v(75.36, 77.36) * mm});
            skArc(sketch, "E221", {"start": v(73.66, 76.8) * mm, "mid": v(74.53, 77.03) * mm, "end": v(75.36, 77.36) * mm});
            skArc(sketch, "E222", {"start": v(73.66, 76.8) * mm, "mid": v(69.53, 76.2) * mm, "end": v(65.35, 76.02) * mm});
            skArc(sketch, "E223", {"start": v(65.35, 76.02) * mm, "mid": v(56.12, 73.62) * mm, "end": v(51.27, 65.4) * mm});
            skArc(sketch, "E224", {"start": v(45.6, 54.1) * mm, "mid": v(49.35, 59.3) * mm, "end": v(51.27, 65.4) * mm});
            skLineSegment(sketch, "E225", {"start": v(45.6, 54.1) * mm, "end": v(22.24, 32.63) * mm});
            skArc(sketch, "E226", {"start": v(15.48, 30) * mm, "mid": v(19.1, 30.68) * mm, "end": v(22.24, 32.63) * mm});
            skLineSegment(sketch, "E227", {"start": v(15.48, 30) * mm, "end": v(-15.48, 30) * mm});
            skArc(sketch, "E228", {"start": v(-22.24, 32.63) * mm, "mid": v(-19.1, 30.68) * mm, "end": v(-15.48, 30) * mm});
            skLineSegment(sketch, "E229", {"start": v(-45.6, 54.1) * mm, "end": v(-22.24, 32.63) * mm});
            skArc(sketch, "E230", {"start": v(-45.6, 54.1) * mm, "mid": v(-49.35, 59.3) * mm, "end": v(-51.27, 65.4) * mm});
            skArc(sketch, "E231", {"start": v(-65.35, 76.02) * mm, "mid": v(-56.12, 73.62) * mm, "end": v(-51.27, 65.4) * mm});
            skArc(sketch, "E232", {"start": v(-73.66, 76.8) * mm, "mid": v(-69.53, 76.2) * mm, "end": v(-65.35, 76.02) * mm});
            skArc(sketch, "E233", {"start": v(-73.66, 76.8) * mm, "mid": v(-74.53, 77.03) * mm, "end": v(-75.36, 77.36) * mm});
            skArc(sketch, "E234", {"start": v(-77.37, 75.37) * mm, "mid": v(-77.07, 77.08) * mm, "end": v(-75.36, 77.36) * mm});
            skArc(sketch, "E235", {"start": v(-77.37, 75.37) * mm, "mid": v(-77.04, 74.54) * mm, "end": v(-76.81, 73.67) * mm});
            skArc(sketch, "E236", {"start": v(-76.81, 73.67) * mm, "mid": v(-76.17, 68.67) * mm, "end": v(-76.14, 63.64) * mm});
            skArc(sketch, "E237", {"start": v(-65.4, 51.27) * mm, "mid": v(-73.08, 55.45) * mm, "end": v(-76.14, 63.64) * mm});
            skArc(sketch, "E238", {"start": v(-65.4, 51.27) * mm, "mid": v(-59.3, 49.35) * mm, "end": v(-54.1, 45.6) * mm});
            skLineSegment(sketch, "E239", {"start": v(-54.1, 45.6) * mm, "end": v(-21.32, 9.92) * mm});
            skArc(sketch, "E240", {"start": v(-20, 6.54) * mm, "mid": v(-20.34, 8.35) * mm, "end": v(-21.32, 9.92) * mm});
            skLineSegment(sketch, "E241", {"start": v(-20, -6.54) * mm, "end": v(-20, 6.54) * mm});
            skArc(sketch, "E242", {"start": v(-20, -6.54) * mm, "mid": v(-20.34, -8.35) * mm, "end": v(-21.32, -9.92) * mm});
            skLineSegment(sketch, "E243", {"start": v(-54.1, -45.6) * mm, "end": v(-21.32, -9.92) * mm});
            skArc(sketch, "E244", {"start": v(-65.4, -51.27) * mm, "mid": v(-59.3, -49.35) * mm, "end": v(-54.1, -45.6) * mm});
            skArc(sketch, "E245", {"start": v(-65.4, -51.27) * mm, "mid": v(-73.08, -55.45) * mm, "end": v(-76.14, -63.64) * mm});
            skArc(sketch, "E246", {"start": v(-76.81, -73.67) * mm, "mid": v(-76.17, -68.67) * mm, "end": v(-76.14, -63.64) * mm});
            skArc(sketch, "E247", {"start": v(-77.37, -75.37) * mm, "mid": v(-77.04, -74.54) * mm, "end": v(-76.81, -73.67) * mm});
            skArc(sketch, "E248", {"start": v(-77.37, -75.37) * mm, "mid": v(-77.07, -77.08) * mm, "end": v(-75.36, -77.36) * mm});
            skArc(sketch, "E249", {"start": v(-73.66, -76.8) * mm, "mid": v(-74.53, -77.03) * mm, "end": v(-75.36, -77.36) * mm});
            skArc(sketch, "E250", {"start": v(-73.66, -76.8) * mm, "mid": v(-69.53, -76.2) * mm, "end": v(-65.35, -76.02) * mm});
            skArc(sketch, "E251", {"start": v(-65.35, -76.02) * mm, "mid": v(-56.12, -73.62) * mm, "end": v(-51.27, -65.4) * mm});
            skArc(sketch, "E252", {"start": v(-45.6, -54.1) * mm, "mid": v(-49.35, -59.3) * mm, "end": v(-51.27, -65.4) * mm});
            skLineSegment(sketch, "E253", {"start": v(-45.6, -54.1) * mm, "end": v(-22.24, -32.63) * mm});
            skArc(sketch, "E254", {"start": v(-22.24, -32.63) * mm, "mid": v(-19.1, -30.68) * mm, "end": v(-15.48, -30) * mm});
            skCircle(sketch, "E255", {"center": v(-63.64, -63.64) * mm, "radius": 3 * mm});
            skCircle(sketch, "E256", {"center": v(63.64, 63.64) * mm, "radius": 3 * mm});
            skCircle(sketch, "E257", {"center": v(63.64, -63.64) * mm, "radius": 3 * mm});
            skCircle(sketch, "E258", {"center": v(-63.64, 63.64) * mm, "radius": 3 * mm});
            skSolve(sketch);
        }
        {
            var Q0;
            Q0=makeQuery(id+"F4.imprint","IMPRINT",FACE,{"disambiguationData":[TD([[makeQuery(id+"F4.imprint","IMPRINT",EDGE,{"derivedFrom":sQuery(id+"F4.wireOp",EDGE,"E175")}),-1.0]])]});
            extrude(context, id + "F5", {"entities" : qUnion([Q0]), "operationType" : NewBodyOperationType.ADD, "depth" : 1.5 * mm, "offsetDistance" : 25 * mm, "hasDraft" : true, "draftAngle" : 70 * degree, "draftPullDirection" : true});
        }
        {
            var Q0;
            Q0=makeQuery(id+"F5.*.draft.opDraft","SPLIT",FACE,{"disambiguationData":[OD(8.0)],"derivedFrom":makeQuery(id+"F5.opExtrude","CAP_FACE",FACE,{"disambiguationData":[OSD([sQuery(id+"F4.wireOp",EDGE,"E175"),sQuery(id+"F4.wireOp",EDGE,"E176"),sQuery(id+"F4.wireOp",EDGE,"E177"),sQuery(id+"F4.wireOp",EDGE,"E178"),sQuery(id+"F4.wireOp",EDGE,"E179"),sQuery(id+"F4.wireOp",EDGE,"E180"),sQuery(id+"F4.wireOp",EDGE,"E181"),sQuery(id+"F4.wireOp",EDGE,"E182"),sQuery(id+"F4.wireOp",EDGE,"E183"),sQuery(id+"F4.wireOp",EDGE,"E184"),sQuery(id+"F4.wireOp",EDGE,"E185"),sQuery(id+"F4.wireOp",EDGE,"E186"),sQuery(id+"F4.wireOp",EDGE,"E187"),sQuery(id+"F4.wireOp",EDGE,"E188"),sQuery(id+"F4.wireOp",EDGE,"E189"),sQuery(id+"F4.wireOp",EDGE,"E190"),sQuery(id+"F4.wireOp",EDGE,"E191"),sQuery(id+"F4.wireOp",EDGE,"E192"),sQuery(id+"F4.wireOp",EDGE,"E193"),sQuery(id+"F4.wireOp",EDGE,"E194"),sQuery(id+"F4.wireOp",EDGE,"E195"),sQuery(id+"F4.wireOp",EDGE,"E196"),sQuery(id+"F4.wireOp",EDGE,"E197"),sQuery(id+"F4.wireOp",EDGE,"E198"),sQuery(id+"F4.wireOp",EDGE,"E199"),sQuery(id+"F4.wireOp",EDGE,"E200"),sQuery(id+"F4.wireOp",EDGE,"E201"),sQuery(id+"F4.wireOp",EDGE,"E202"),sQuery(id+"F4.wireOp",EDGE,"E203"),sQuery(id+"F4.wireOp",EDGE,"E204"),sQuery(id+"F4.wireOp",EDGE,"E205"),sQuery(id+"F4.wireOp",EDGE,"E206"),sQuery(id+"F4.wireOp",EDGE,"E207"),sQuery(id+"F4.wireOp",EDGE,"E208"),sQuery(id+"F4.wireOp",EDGE,"E209"),sQuery(id+"F4.wireOp",EDGE,"E210"),sQuery(id+"F4.wireOp",EDGE,"E211"),sQuery(id+"F4.wireOp",EDGE,"E212"),sQuery(id+"F4.wireOp",EDGE,"E213"),sQuery(id+"F4.wireOp",EDGE,"E214"),sQuery(id+"F4.wireOp",EDGE,"E215"),sQuery(id+"F4.wireOp",EDGE,"E216"),sQuery(id+"F4.wireOp",EDGE,"E217"),sQuery(id+"F4.wireOp",EDGE,"E218"),sQuery(id+"F4.wireOp",EDGE,"E219"),sQuery(id+"F4.wireOp",EDGE,"E220"),sQuery(id+"F4.wireOp",EDGE,"E221"),sQuery(id+"F4.wireOp",EDGE,"E222"),sQuery(id+"F4.wireOp",EDGE,"E223"),sQuery(id+"F4.wireOp",EDGE,"E224"),sQuery(id+"F4.wireOp",EDGE,"E225"),sQuery(id+"F4.wireOp",EDGE,"E226"),sQuery(id+"F4.wireOp",EDGE,"E227"),sQuery(id+"F4.wireOp",EDGE,"E228"),sQuery(id+"F4.wireOp",EDGE,"E229"),sQuery(id+"F4.wireOp",EDGE,"E230"),sQuery(id+"F4.wireOp",EDGE,"E231"),sQuery(id+"F4.wireOp",EDGE,"E232"),sQuery(id+"F4.wireOp",EDGE,"E233"),sQuery(id+"F4.wireOp",EDGE,"E234"),sQuery(id+"F4.wireOp",EDGE,"E235"),sQuery(id+"F4.wireOp",EDGE,"E236"),sQuery(id+"F4.wireOp",EDGE,"E237"),sQuery(id+"F4.wireOp",EDGE,"E238"),sQuery(id+"F4.wireOp",EDGE,"E239"),sQuery(id+"F4.wireOp",EDGE,"E240"),sQuery(id+"F4.wireOp",EDGE,"E241"),sQuery(id+"F4.wireOp",EDGE,"E242"),sQuery(id+"F4.wireOp",EDGE,"E243"),sQuery(id+"F4.wireOp",EDGE,"E244"),sQuery(id+"F4.wireOp",EDGE,"E245"),sQuery(id+"F4.wireOp",EDGE,"E246"),sQuery(id+"F4.wireOp",EDGE,"E247"),sQuery(id+"F4.wireOp",EDGE,"E248"),sQuery(id+"F4.wireOp",EDGE,"E249"),sQuery(id+"F4.wireOp",EDGE,"E250"),sQuery(id+"F4.wireOp",EDGE,"E251"),sQuery(id+"F4.wireOp",EDGE,"E252"),sQuery(id+"F4.wireOp",EDGE,"E253"),sQuery(id+"F4.wireOp",EDGE,"E254"),sQuery(id+"F4.wireOp",EDGE,"E255"),sQuery(id+"F4.wireOp",EDGE,"E256"),sQuery(id+"F4.wireOp",EDGE,"E257"),sQuery(id+"F4.wireOp",EDGE,"E258")])],"isStart":false})});
            var sketch = newSketch(context, id + "F6", { "sketchPlane" : qUnion([Q0])});
            skCircle(sketch, "E259.0", {"center": v(-63.64, 63.64) * mm, "radius": 3 * mm, "construction": true});
            skCircle(sketch, "E260.0", {"center": v(-63.64, -63.64) * mm, "radius": 3 * mm, "construction": true});
            skCircle(sketch, "E261.0", {"center": v(63.64, 63.64) * mm, "radius": 3 * mm, "construction": true});
            skCircle(sketch, "E261.1", {"center": v(63.64, -63.64) * mm, "radius": 3 * mm, "construction": true});
            skLineSegment(sketch, "E262", {"start": v(-63.64, 63.64) * mm, "end": v(63.64, -63.64) * mm, "construction": true});
            skLineSegment(sketch, "E263", {"start": v(63.64, 63.64) * mm, "end": v(-63.64, -63.64) * mm, "construction": true});
            skLineSegment(sketch, "E264", {"start": v(-57.53, 55.55) * mm, "end": v(-18.64, 16.66) * mm});
            skPoint(sketch, "E265", {"position": v(0, 0) * mm});
            skLineSegment(sketch, "E266.MirrorCS", {"start": v(-55.55, 57.53) * mm, "end": v(-16.66, 18.64) * mm});
            skLineSegment(sketch, "E267", {"start": v(-55.55, 57.53) * mm, "end": v(-57.53, 55.55) * mm});
            skLineSegment(sketch, "E268", {"start": v(-18.64, 16.66) * mm, "end": v(-16.66, 18.64) * mm});
            skLineSegment(sketch, "E269.MirrorCS", {"start": v(16.66, -18.64) * mm, "end": v(18.64, -16.66) * mm});
            skLineSegment(sketch, "E270.MirrorCS", {"start": v(57.53, -55.55) * mm, "end": v(55.55, -57.53) * mm});
            skLineSegment(sketch, "E271.MirrorCS", {"start": v(57.53, -55.55) * mm, "end": v(18.64, -16.66) * mm});
            skLineSegment(sketch, "E272.MirrorCS", {"start": v(55.55, -57.53) * mm, "end": v(16.66, -18.64) * mm});
            skLineSegment(sketch, "E273", {"start": v(0, 0) * mm, "end": v(0, -62.95) * mm, "construction": true});
            skLineSegment(sketch, "E274.MirrorCS", {"start": v(-16.66, -18.64) * mm, "end": v(-18.64, -16.66) * mm});
            skLineSegment(sketch, "E275.MirrorCS", {"start": v(-57.53, -55.55) * mm, "end": v(-55.55, -57.53) * mm});
            skLineSegment(sketch, "E276.MirrorCS", {"start": v(-55.55, -57.53) * mm, "end": v(-16.66, -18.64) * mm});
            skLineSegment(sketch, "E277.MirrorCS", {"start": v(-57.53, -55.55) * mm, "end": v(-18.64, -16.66) * mm});
            skLineSegment(sketch, "E278.MirrorCS", {"start": v(18.64, 16.66) * mm, "end": v(16.66, 18.64) * mm});
            skLineSegment(sketch, "E279.MirrorCS", {"start": v(55.55, 57.53) * mm, "end": v(57.53, 55.55) * mm});
            skLineSegment(sketch, "E280.MirrorCS", {"start": v(57.53, 55.55) * mm, "end": v(18.64, 16.66) * mm});
            skLineSegment(sketch, "E281.MirrorCS", {"start": v(55.55, 57.53) * mm, "end": v(16.66, 18.64) * mm});
            skSolve(sketch);
        }
        {
            var Q0;
            Q0=makeQuery(id+"F6.imprint","IMPRINT",FACE,{"disambiguationData":[TD([[makeQuery(id+"F6.imprint","IMPRINT",EDGE,{"derivedFrom":sQuery(id+"F6.wireOp",EDGE,"E278.MirrorCS")}),-1.0]])]});
            var Q1;
            Q1=makeQuery(id+"F6.imprint","IMPRINT",FACE,{"disambiguationData":[TD([[makeQuery(id+"F6.imprint","IMPRINT",EDGE,{"derivedFrom":sQuery(id+"F6.wireOp",EDGE,"E264")}),1.0]])]});
            var Q2;
            Q2=makeQuery(id+"F6.imprint","IMPRINT",FACE,{"disambiguationData":[TD([[makeQuery(id+"F6.imprint","IMPRINT",EDGE,{"derivedFrom":sQuery(id+"F6.wireOp",EDGE,"E274.MirrorCS")}),1.0]])]});
            var Q3;
            Q3=makeQuery(id+"F6.imprint","IMPRINT",FACE,{"disambiguationData":[TD([[makeQuery(id+"F6.imprint","IMPRINT",EDGE,{"derivedFrom":sQuery(id+"F6.wireOp",EDGE,"E269.MirrorCS")}),-1.0]])]});
            extrude(context, id + "F7", {"entities" : qUnion([Q0, Q1, Q2, Q3]), "operationType" : NewBodyOperationType.REMOVE, "oppositeDirection" : true, "depth" : 3 * mm, "offsetDistance" : 25 * mm});
        }
        {
            var Q0;
            Q0=makeQuery(id+"F7.boolean.opBoolean","COPY",EDGE,{"derivedFrom":makeQuery(id+"F7.opExtrude","CAP_EDGE",EDGE,{"disambiguationData":[OSD([sQuery(id+"F6.wireOp",EDGE,"E281.MirrorCS")])],"isStart":false})});
            var Q1;
            Q1=makeQuery(id+"F7.boolean.opBoolean","COPY",EDGE,{"derivedFrom":makeQuery(id+"F7.opExtrude","CAP_EDGE",EDGE,{"disambiguationData":[OSD([sQuery(id+"F6.wireOp",EDGE,"E280.MirrorCS")])],"isStart":false})});
            var Q2;
            Q2=makeQuery(id+"F7.boolean.opBoolean","COPY",EDGE,{"derivedFrom":makeQuery(id+"F7.opExtrude","CAP_EDGE",EDGE,{"disambiguationData":[OSD([sQuery(id+"F6.wireOp",EDGE,"E266.MirrorCS")])],"isStart":false})});
            var Q3;
            Q3=makeQuery(id+"F7.boolean.opBoolean","COPY",EDGE,{"derivedFrom":makeQuery(id+"F7.opExtrude","CAP_EDGE",EDGE,{"disambiguationData":[OSD([sQuery(id+"F6.wireOp",EDGE,"E264")])],"isStart":false})});
            var Q4;
            Q4=makeQuery(id+"F7.boolean.opBoolean","COPY",EDGE,{"derivedFrom":makeQuery(id+"F7.opExtrude","CAP_EDGE",EDGE,{"disambiguationData":[OSD([sQuery(id+"F6.wireOp",EDGE,"E277.MirrorCS")])],"isStart":false})});
            var Q5;
            Q5=makeQuery(id+"F7.boolean.opBoolean","COPY",EDGE,{"derivedFrom":makeQuery(id+"F7.opExtrude","CAP_EDGE",EDGE,{"disambiguationData":[OSD([sQuery(id+"F6.wireOp",EDGE,"E276.MirrorCS")])],"isStart":false})});
            var Q6;
            Q6=makeQuery(id+"F7.boolean.opBoolean","COPY",EDGE,{"derivedFrom":makeQuery(id+"F7.opExtrude","CAP_EDGE",EDGE,{"disambiguationData":[OSD([sQuery(id+"F6.wireOp",EDGE,"E272.MirrorCS")])],"isStart":false})});
            var Q7;
            Q7=makeQuery(id+"F7.boolean.opBoolean","COPY",EDGE,{"derivedFrom":makeQuery(id+"F7.opExtrude","CAP_EDGE",EDGE,{"disambiguationData":[OSD([sQuery(id+"F6.wireOp",EDGE,"E271.MirrorCS")])],"isStart":false})});
            fillet(context, id + "F8", {"entities" : qUnion([Q0, Q1, Q2, Q3, Q4, Q5, Q6, Q7]), "tangentPropagation" : true, "radius" : 1.6 * mm, "defaultsChanged" : true, "vertexSettings" : [], "allowEdgeOverflow" : false});
        }
        {
            var Q0;
            Q0=makeQuery(id+"F5.*.draft.opDraft","SPLIT",FACE,{"disambiguationData":[OD(8.0)],"derivedFrom":makeQuery(id+"F5.opExtrude","CAP_FACE",FACE,{"disambiguationData":[OSD([sQuery(id+"F4.wireOp",EDGE,"E175"),sQuery(id+"F4.wireOp",EDGE,"E176"),sQuery(id+"F4.wireOp",EDGE,"E177"),sQuery(id+"F4.wireOp",EDGE,"E178"),sQuery(id+"F4.wireOp",EDGE,"E179"),sQuery(id+"F4.wireOp",EDGE,"E180"),sQuery(id+"F4.wireOp",EDGE,"E181"),sQuery(id+"F4.wireOp",EDGE,"E182"),sQuery(id+"F4.wireOp",EDGE,"E183"),sQuery(id+"F4.wireOp",EDGE,"E184"),sQuery(id+"F4.wireOp",EDGE,"E185"),sQuery(id+"F4.wireOp",EDGE,"E186"),sQuery(id+"F4.wireOp",EDGE,"E187"),sQuery(id+"F4.wireOp",EDGE,"E188"),sQuery(id+"F4.wireOp",EDGE,"E189"),sQuery(id+"F4.wireOp",EDGE,"E190"),sQuery(id+"F4.wireOp",EDGE,"E191"),sQuery(id+"F4.wireOp",EDGE,"E192"),sQuery(id+"F4.wireOp",EDGE,"E193"),sQuery(id+"F4.wireOp",EDGE,"E194"),sQuery(id+"F4.wireOp",EDGE,"E195"),sQuery(id+"F4.wireOp",EDGE,"E196"),sQuery(id+"F4.wireOp",EDGE,"E197"),sQuery(id+"F4.wireOp",EDGE,"E198"),sQuery(id+"F4.wireOp",EDGE,"E199"),sQuery(id+"F4.wireOp",EDGE,"E200"),sQuery(id+"F4.wireOp",EDGE,"E201"),sQuery(id+"F4.wireOp",EDGE,"E202"),sQuery(id+"F4.wireOp",EDGE,"E203"),sQuery(id+"F4.wireOp",EDGE,"E204"),sQuery(id+"F4.wireOp",EDGE,"E205"),sQuery(id+"F4.wireOp",EDGE,"E206"),sQuery(id+"F4.wireOp",EDGE,"E207"),sQuery(id+"F4.wireOp",EDGE,"E208"),sQuery(id+"F4.wireOp",EDGE,"E209"),sQuery(id+"F4.wireOp",EDGE,"E210"),sQuery(id+"F4.wireOp",EDGE,"E211"),sQuery(id+"F4.wireOp",EDGE,"E212"),sQuery(id+"F4.wireOp",EDGE,"E213"),sQuery(id+"F4.wireOp",EDGE,"E214"),sQuery(id+"F4.wireOp",EDGE,"E215"),sQuery(id+"F4.wireOp",EDGE,"E216"),sQuery(id+"F4.wireOp",EDGE,"E217"),sQuery(id+"F4.wireOp",EDGE,"E218"),sQuery(id+"F4.wireOp",EDGE,"E219"),sQuery(id+"F4.wireOp",EDGE,"E220"),sQuery(id+"F4.wireOp",EDGE,"E221"),sQuery(id+"F4.wireOp",EDGE,"E222"),sQuery(id+"F4.wireOp",EDGE,"E223"),sQuery(id+"F4.wireOp",EDGE,"E224"),sQuery(id+"F4.wireOp",EDGE,"E225"),sQuery(id+"F4.wireOp",EDGE,"E226"),sQuery(id+"F4.wireOp",EDGE,"E227"),sQuery(id+"F4.wireOp",EDGE,"E228"),sQuery(id+"F4.wireOp",EDGE,"E229"),sQuery(id+"F4.wireOp",EDGE,"E230"),sQuery(id+"F4.wireOp",EDGE,"E231"),sQuery(id+"F4.wireOp",EDGE,"E232"),sQuery(id+"F4.wireOp",EDGE,"E233"),sQuery(id+"F4.wireOp",EDGE,"E234"),sQuery(id+"F4.wireOp",EDGE,"E235"),sQuery(id+"F4.wireOp",EDGE,"E236"),sQuery(id+"F4.wireOp",EDGE,"E237"),sQuery(id+"F4.wireOp",EDGE,"E238"),sQuery(id+"F4.wireOp",EDGE,"E239"),sQuery(id+"F4.wireOp",EDGE,"E240"),sQuery(id+"F4.wireOp",EDGE,"E241"),sQuery(id+"F4.wireOp",EDGE,"E242"),sQuery(id+"F4.wireOp",EDGE,"E243"),sQuery(id+"F4.wireOp",EDGE,"E244"),sQuery(id+"F4.wireOp",EDGE,"E245"),sQuery(id+"F4.wireOp",EDGE,"E246"),sQuery(id+"F4.wireOp",EDGE,"E247"),sQuery(id+"F4.wireOp",EDGE,"E248"),sQuery(id+"F4.wireOp",EDGE,"E249"),sQuery(id+"F4.wireOp",EDGE,"E250"),sQuery(id+"F4.wireOp",EDGE,"E251"),sQuery(id+"F4.wireOp",EDGE,"E252"),sQuery(id+"F4.wireOp",EDGE,"E253"),sQuery(id+"F4.wireOp",EDGE,"E254"),sQuery(id+"F4.wireOp",EDGE,"E255"),sQuery(id+"F4.wireOp",EDGE,"E256"),sQuery(id+"F4.wireOp",EDGE,"E257"),sQuery(id+"F4.wireOp",EDGE,"E258")])],"isStart":false})});
            var sketch = newSketch(context, id + "F9", { "sketchPlane" : qUnion([Q0])});
            skCircle(sketch, "E282.0", {"center": v(15.25, 15.25) * mm, "radius": 1.5 * mm, "construction": true});
            skCircle(sketch, "E282.1", {"center": v(17, 26) * mm, "radius": 1.5 * mm, "construction": true});
            skCircle(sketch, "E282.2", {"center": v(-17, 26) * mm, "radius": 1.5 * mm, "construction": true});
            skCircle(sketch, "E282.3", {"center": v(-15.25, 15.25) * mm, "radius": 1.5 * mm, "construction": true});
            skCircle(sketch, "E282.4", {"center": v(-15.25, -15.25) * mm, "radius": 1.5 * mm, "construction": true});
            skCircle(sketch, "E282.5", {"center": v(-17, -26) * mm, "radius": 1.5 * mm, "construction": true});
            skCircle(sketch, "E282.6", {"center": v(17, -26) * mm, "radius": 1.5 * mm, "construction": true});
            skCircle(sketch, "E282.7", {"center": v(15.25, -15.25) * mm, "radius": 1.5 * mm, "construction": true});
            skCircle(sketch, "E283", {"center": v(-17, 26) * mm, "radius": 3 * mm});
            skCircle(sketch, "E284", {"center": v(17, 26) * mm, "radius": 3 * mm});
            skCircle(sketch, "E285", {"center": v(15.25, 15.25) * mm, "radius": 3 * mm});
            skCircle(sketch, "E286", {"center": v(-15.25, 15.25) * mm, "radius": 3 * mm});
            skCircle(sketch, "E287", {"center": v(-15.25, -15.25) * mm, "radius": 3 * mm});
            skCircle(sketch, "E288", {"center": v(15.25, -15.25) * mm, "radius": 3 * mm});
            skCircle(sketch, "E289", {"center": v(17, -26) * mm, "radius": 3 * mm});
            skCircle(sketch, "E290", {"center": v(-17, -26) * mm, "radius": 3 * mm});
            skSolve(sketch);
        }
        {
            var Q0;
            Q0 = qSketchRegion(id + "F9", true);
            extrude(context, id + "F10", {"entities" : qUnion([Q0]), "operationType" : NewBodyOperationType.REMOVE, "oppositeDirection" : true, "depth" : 1.5 * mm, "offsetDistance" : 25 * mm});
        }
    });
